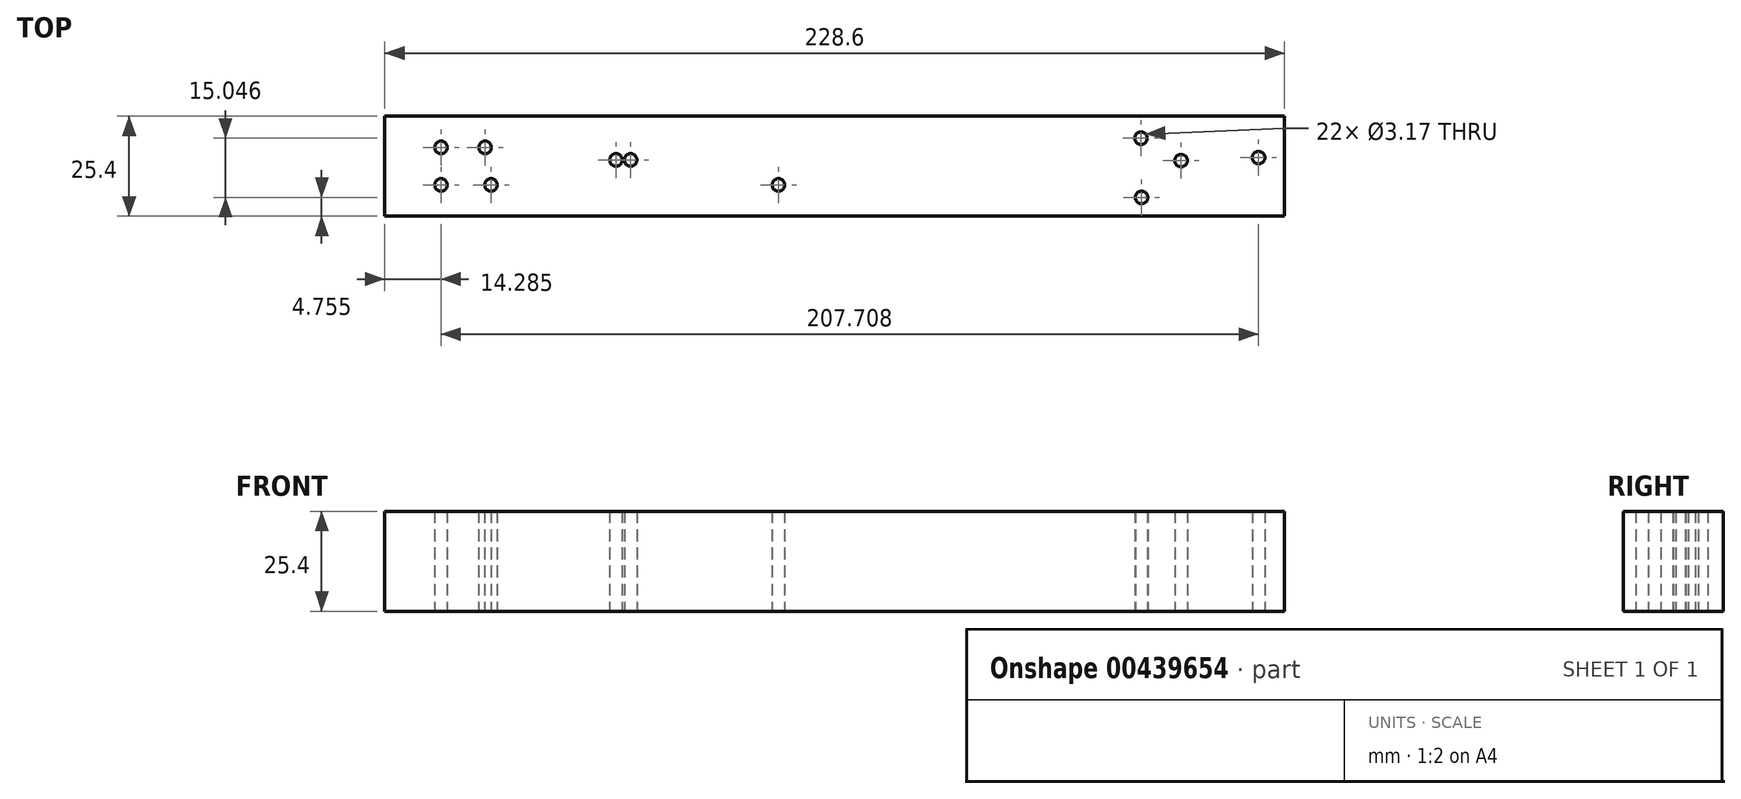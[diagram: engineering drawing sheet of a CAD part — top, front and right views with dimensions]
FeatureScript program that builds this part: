
annotation { "Feature Type Name" : "Feature", "Feature Type Description" : "" }
export const myFeature = defineFeature(function(context is Context, id is Id, definition is map)
    precondition{}
    {
        {
            var Q0;
            Q0=qCreatedBy(makeId("Top.planeOp"),FACE);
            var sketch = newSketch(context, id + "F0", { "sketchPlane" : qUnion([Q0])});
            skLineSegment(sketch, "E0.bottom", {"start": v(-115.6, 0.67) * mm, "end": v(113, 0.67) * mm});
            skLineSegment(sketch, "E0.top", {"start": v(-115.6, -24.73) * mm, "end": v(113, -24.73) * mm});
            skLineSegment(sketch, "E0.left", {"start": v(-115.6, 0.67) * mm, "end": v(-115.6, -24.73) * mm});
            skLineSegment(sketch, "E0.right", {"start": v(113, 0.67) * mm, "end": v(113, -24.73) * mm});
            skCircle(sketch, "E1", {"center": v(-101.31, -7.27) * mm, "radius": 1.59 * mm});
            skCircle(sketch, "E2", {"center": v(-101.31, -16.8) * mm, "radius": 1.59 * mm});
            skCircle(sketch, "E3", {"center": v(-90.11, -7.27) * mm, "radius": 1.59 * mm});
            skCircle(sketch, "E4", {"center": v(-88.61, -16.8) * mm, "radius": 1.59 * mm});
            skCircle(sketch, "E5", {"center": v(-53.14, -10.44) * mm, "radius": 1.59 * mm});
            skCircle(sketch, "E6", {"center": v(-56.86, -10.44) * mm, "radius": 1.59 * mm});
            skCircle(sketch, "E7", {"center": v(-15.59, -16.8) * mm, "radius": 1.59 * mm});
            skCircle(sketch, "E8", {"center": v(76.52, -4.93) * mm, "radius": 1.59 * mm});
            skCircle(sketch, "E9", {"center": v(76.66, -19.97) * mm, "radius": 1.59 * mm});
            skCircle(sketch, "E10", {"center": v(86.7, -10.62) * mm, "radius": 1.59 * mm});
            skCircle(sketch, "E11", {"center": v(106.4, -9.86) * mm, "radius": 1.59 * mm});
            skSolve(sketch);
        }
        {
            var Q0;
            Q0=makeQuery(id+"F0.imprint","IMPRINT",FACE,{"disambiguationData":[TD([[makeQuery(id+"F0.imprint","IMPRINT",EDGE,{"derivedFrom":sQuery(id+"F0.wireOp",EDGE,"E0.bottom")}),-1.0]])]});
            extrude(context, id + "F1", {"entities" : qUnion([Q0]), "depth" : 25.4 * mm});
        }
    });
